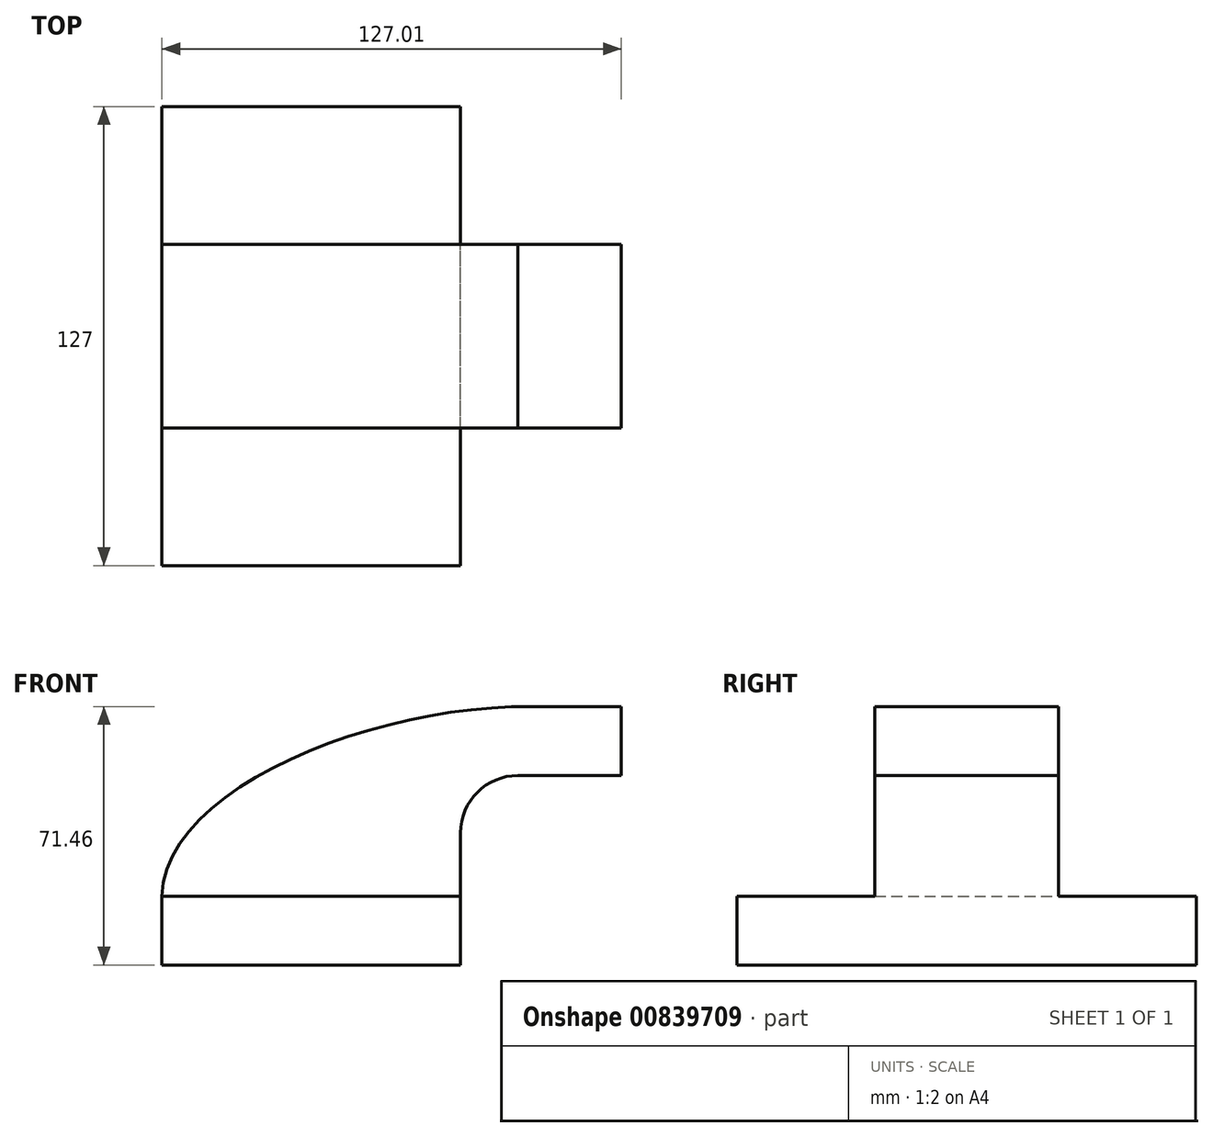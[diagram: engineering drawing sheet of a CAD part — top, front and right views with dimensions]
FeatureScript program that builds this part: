
annotation { "Feature Type Name" : "Feature", "Feature Type Description" : "" }
export const myFeature = defineFeature(function(context is Context, id is Id, definition is map)
    precondition{}
    {
        {
            var Q0;
            Q0=qCreatedBy(makeId("Front.planeOp"),FACE);
            var sketch = newSketch(context, id + "F0", { "sketchPlane" : qUnion([Q0])});
            skLineSegment(sketch, "E0.bottom", {"start": v(41.28, -9.52) * mm, "end": v(-41.28, -9.53) * mm});
            skLineSegment(sketch, "E0.top", {"start": v(41.28, 9.53) * mm, "end": v(-41.28, 9.52) * mm});
            skLineSegment(sketch, "E0.left", {"start": v(41.28, -9.52) * mm, "end": v(41.28, 9.53) * mm});
            skLineSegment(sketch, "E0.right", {"start": v(-41.28, -9.53) * mm, "end": v(-41.28, 9.52) * mm});
            skPoint(sketch, "E0.middle", {"position": v(0, 0) * mm});
            skLineSegment(sketch, "E1", {"start": v(41.28, 9.53) * mm, "end": v(41.28, 27) * mm});
            skArc(sketch, "E2", {"start": v(41.28, 27) * mm, "mid": v(45.92, 38.23) * mm, "end": v(57.15, 42.88) * mm});
            skLineSegment(sketch, "E3", {"start": v(57.15, 42.88) * mm, "end": v(85.72, 42.88) * mm});
            skLineSegment(sketch, "E4.bottom", {"start": v(111.12, 38.1) * mm, "end": v(60.32, 38.1) * mm});
            skLineSegment(sketch, "E4.top", {"start": v(111.12, 66.68) * mm, "end": v(60.32, 66.68) * mm});
            skLineSegment(sketch, "E4.left", {"start": v(111.12, 38.1) * mm, "end": v(111.12, 66.68) * mm});
            skLineSegment(sketch, "E4.right", {"start": v(60.32, 38.1) * mm, "end": v(60.32, 66.68) * mm});
            skPoint(sketch, "E4.middle", {"position": v(85.72, 52.39) * mm});
            skLineSegment(sketch, "E5.0", {"start": v(57.15, 61.93) * mm, "end": v(85.72, 61.93) * mm});
            skArc(sketch, "E5.1", {"start": v(22.23, 27) * mm, "mid": v(32.45, 51.7) * mm, "end": v(57.15, 61.93) * mm});
            skLineSegment(sketch, "E5.2", {"start": v(22.23, 9.53) * mm, "end": v(22.23, 27) * mm});
            skLineSegment(sketch, "E6", {"start": v(85.72, 42.88) * mm, "end": v(85.72, 66.68) * mm});
            skFitSpline(sketch, "E7", {"points": [v(-41.28, 9.52) * mm, v(57.15, 61.93) * mm], "startDerivative": vector(2.35, 89.04) * mm, "endDerivative": vector(125.4, 2.32) * mm});
            skSolve(sketch);
        }
        {
            var Q0;
            Q0=makeQuery(id+"F0.imprint","IMPRINT",FACE,{"disambiguationData":[TD([[makeQuery(id+"F0.imprint","IMPRINT",EDGE,{"derivedFrom":sQuery(id+"F0.wireOp",EDGE,"E0.bottom")}),-1.0]])]});
            extrude(context, id + "F1", {"entities" : qUnion([Q0]), "endBound" : BoundingType.SYMMETRIC, "depth" : 127 * mm, "offsetDistance" : 25.4 * mm});
        }
        {
            var Q0;
            {var subQ8=sQuery(id+"F0.wireOp",EDGE,"E1");Q0=makeQuery(id+"F0.imprint","IMPRINT",FACE,{"disambiguationData":[TD([[makeQuery(id+"F0.imprint","IMPRINT",EDGE,{"derivedFrom":subQ8}),1.0]])]});}
            var Q1;
            {var subQ0=sQuery(id+"F0.wireOp",EDGE,"E6");var subQ1=sQuery(id+"F0.wireOp",EDGE,"E3");var subQ2=makeQuery(id+"F0.imprint","INTERSECT",VERTEX,{"derivedFrom":[subQ1,subQ0]});Q1=makeQuery(id+"F0.imprint","IMPRINT",FACE,{"disambiguationData":[TD([[makeQuery(id+"F0.imprint","IMPRINT",EDGE,{"disambiguationData":[TD([[subQ2,1.0]])],"derivedFrom":subQ1}),1.0]])]});}
            extrude(context, id + "F2", {"entities" : qUnion([Q0, Q1]), "operationType" : NewBodyOperationType.ADD, "endBound" : BoundingType.SYMMETRIC, "depth" : 50.8 * mm, "offsetDistance" : 25.4 * mm});
        }
        {
            var Q0;
            {var subQ3=sQuery(id+"F0.wireOp",EDGE,"E5.2");Q0=makeQuery(id+"F0.imprint","IMPRINT",FACE,{"disambiguationData":[TD([[makeQuery(id+"F0.imprint","IMPRINT",EDGE,{"derivedFrom":subQ3}),1.0]])]});}
            extrude(context, id + "F3", {"entities" : qUnion([Q0]), "operationType" : NewBodyOperationType.ADD, "endBound" : BoundingType.SYMMETRIC, "depth" : 50.8 * mm, "offsetDistance" : 25.4 * mm});
        }
    });
